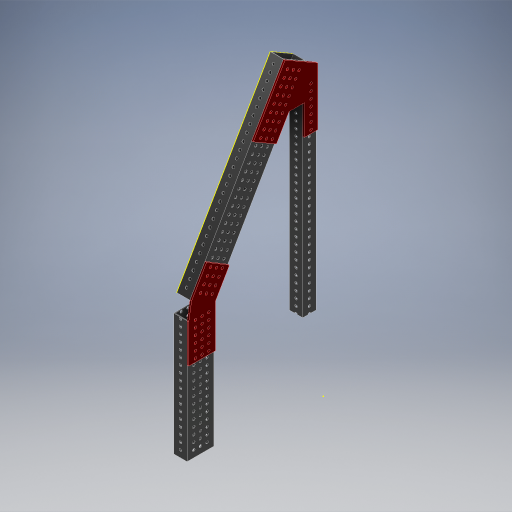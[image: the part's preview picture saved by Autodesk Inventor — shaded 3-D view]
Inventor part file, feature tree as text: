
AUTODESK INVENTOR PART (.ipt)
format: ipt  version: 2024.2 (Build 282272000, 272)  size: 1,317,888 bytes
history: native  units: in
note: dims shown in document units (in); Inventor stores cm internally (conversion verified against a paired STEP export)
features: extrude x12, projected_geometry x11, sketch x10, other x5
ambient origin geometry x8: Origin, YZ Plane, XZ Plane, XY Plane, X Axis, Y Axis, Z Axis, Center Point
bodies: Body1 (feature_tree), Body2 (feature_tree), Body3 (feature_tree), Body4 (feature_tree), Body5 (feature_tree)
feature tree (38):
  other  "2024-210-001-Shooter-Beam"
  sketch  "Sketch1"  dims[d25=9.12in d26=2.0in]
  extrude  "Extrusion1"  Depth=2.0in
  extrude  "Extrusion2"  Depth=2.0in
  extrude  "Extrusion3"  TaperAngle=60.0deg  [1 undecoded]
  extrude  "Extrusion4"  Depth=2.0in
  extrude  "Extrusion5"  Depth=6.654in
  extrude  "Extrusion6"  Depth=2.0in
  sketch  "Sketch5"  dims[d43=1.0in d44=6.654in]
  extrude  "Extrusion7"  Depth=2.0in
  extrude  "Extrusion8"  Depth=0.5in
  extrude  "Extrusion9"  Depth=17.5in
  extrude  "Extrusion10"  Depth=1.0in TaperAngle=0.0deg
  extrude  "Extrusion12"  Depth=1.0in TaperAngle=0.0deg
  extrude  "Extrusion13"  Depth=2.0in
  sketch  "Sketch10"  dims[d71=1.0in d72=0.0in d73=1.0in d74=0.0in d85=1.0in d86=0.0in d87=0.196in d88=0.5in d89=0.5in d90=1.1811in d92=0.5in d93=7.0866in d95=0.5in d98=0.0625in d99=9.5625in d100=0.0in d101=0.0625in d102=9.5625in d103=0.0in d104=0.196in d105=0.5in d106=0.5in d107=13.7795in d109=0.5in d110=0.3937in d112=1.0in d114=0.0625in d115=1.0in d116=0.0in d117=2.87in d118=2.25in d119=2.25in d120=1.5in d122=4.75in d123=0.125in d124=0.0in d125=0.125in d126=0.0in d130=0.196in d131=0.5in d132=0.5in d133=13.7795in d135=0.5in d136=0.3937in d138=1.0in d140=0.125in d141=0.0in d142=0.196in d143=0.5in d144=0.5in d145=10.6299in d147=0.5in d148=0.3937in d150=1.0in d152=1.0in d153=0.0in d166=0.196in d167=0.5in d168=0.5in d169=7.0866in d171=0.5in d172=0.3937in d174=1.0in d176=1.0in d177=0.0in d178=2.0in d179=0.0in d127=0.5in d128=0.0344in]
  other  "2024-210-003-Front-Angle"
  other  "2024-210-002-Backright-Support"
  sketch  "Sketch2"  dims[d29=2.0in d34=0.25in]
  projected_geometry  "Projected Loop1"
  sketch  "Sketch3"  dims[d37=14.0in d39=60.0deg]
  projected_geometry  "Projected Loop2"
  sketch  "Sketch4"  dims[d41=1.0in d42=2.0in]
  projected_geometry  "Projected Loop3"
  projected_geometry  "Projected Loop4"
  projected_geometry  "Projected Loop5"
  projected_geometry  "Projected Loop6"
  other  "2024-210-004-Back-Gusset"
  other  "2024-210-005-Front-Gusset"
  sketch  "Sketch6"  dims[d45=2.0in d46=17.346in]
  projected_geometry  "Projected Loop7"
  sketch  "Sketch7"  dims[d48=0.196in d59=2.0in]
  projected_geometry  "Projected Loop8"
  sketch  "Sketch8"  dims[d60=0.5in d61=0.5in]
  projected_geometry  "Projected Loop9"
  sketch  "Sketch9"  dims[d62=1.1811in d64=0.5in d65=10.6299in d67=0.5in d70=17.5in]
  projected_geometry  "Projected Loop10"
  projected_geometry  "Projected Loop11"
note: 1 required parameter value undecoded (feature->parameter linkage not recoverable at this tier; creation-order binding heuristic only, values carry confidence <= 0.55)
